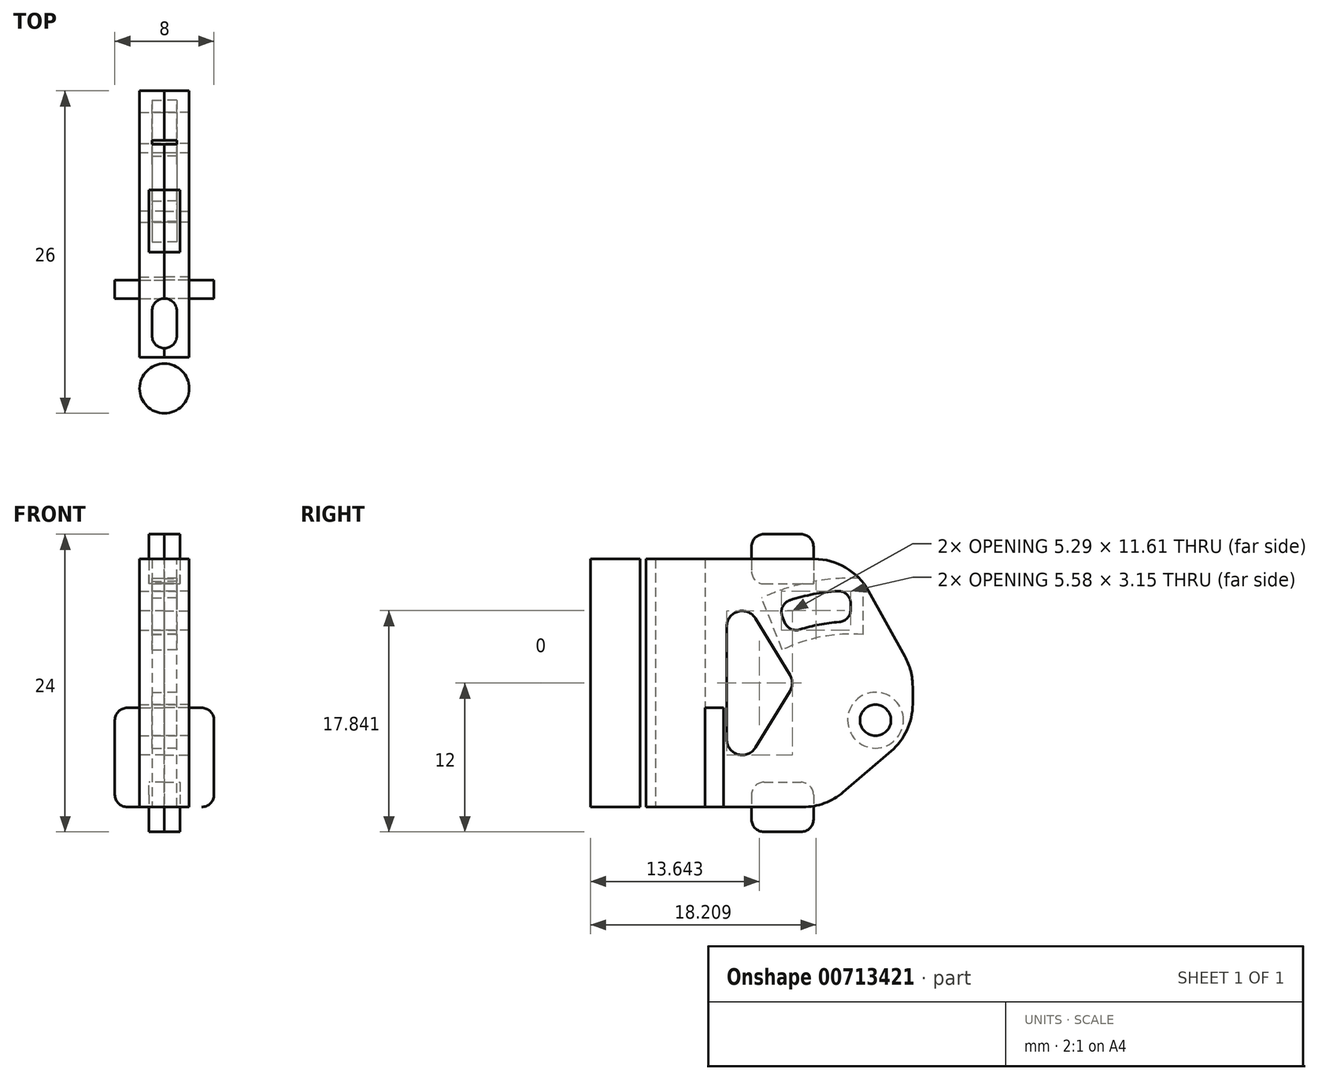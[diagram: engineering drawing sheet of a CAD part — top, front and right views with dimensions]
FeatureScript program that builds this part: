
annotation { "Feature Type Name" : "Feature", "Feature Type Description" : "" }
export const myFeature = defineFeature(function(context is Context, id is Id, definition is map)
    precondition{}
    {
        {
            var Q0;
            Q0=qCreatedBy(makeId("Right.planeOp"),FACE);
            var sketch = newSketch(context, id + "F0", { "sketchPlane" : qUnion([Q0])});
            skLineSegment(sketch, "E0.bottom", {"start": v(2.5, 0) * mm, "end": v(7, 0) * mm});
            skLineSegment(sketch, "E0.top", {"start": v(2.5, 20) * mm, "end": v(7, 20) * mm});
            skLineSegment(sketch, "E0.left", {"start": v(2.5, 0) * mm, "end": v(2.5, 20) * mm});
            skLineSegment(sketch, "E0.right", {"start": v(7, 0) * mm, "end": v(7, 20) * mm});
            skLineSegment(sketch, "E1", {"start": v(17, 0) * mm, "end": v(7, 0) * mm});
            skLineSegment(sketch, "E2", {"start": v(17, 0) * mm, "end": v(24, 6) * mm});
            skLineSegment(sketch, "E3", {"start": v(19, 20) * mm, "end": v(7, 20) * mm});
            skLineSegment(sketch, "E4", {"start": v(24, 6) * mm, "end": v(24, 11) * mm});
            skLineSegment(sketch, "E5", {"start": v(24, 11) * mm, "end": v(19, 20) * mm});
            skLineSegment(sketch, "E6", {"start": v(9, 19) * mm, "end": v(9, 1) * mm});
            skLineSegment(sketch, "E7", {"start": v(9, 1) * mm, "end": v(14.5, 10) * mm});
            skLineSegment(sketch, "E8", {"start": v(14.5, 10) * mm, "end": v(9, 19) * mm});
            skCircle(sketch, "E9", {"center": v(21, 7) * mm, "radius": 1.25 * mm});
            skArc(sketch, "E10", {"start": v(19, 17.45) * mm, "mid": v(16, 17.17) * mm, "end": v(13.1, 16.32) * mm});
            skArc(sketch, "E11", {"start": v(19, 14.95) * mm, "mid": v(16.47, 14.7) * mm, "end": v(14.03, 14) * mm});
            skLineSegment(sketch, "E12", {"start": v(19, 14.95) * mm, "end": v(19, 17.45) * mm});
            skLineSegment(sketch, "E13", {"start": v(14.03, 14) * mm, "end": v(13.1, 16.32) * mm});
            skLineSegment(sketch, "E14", {"start": v(9, 19) * mm, "end": v(9, 20) * mm, "construction": true});
            skLineSegment(sketch, "E15", {"start": v(9, 1) * mm, "end": v(9, 0) * mm, "construction": true});
            skLineSegment(sketch, "E16.bottom", {"start": v(-2.5, 0) * mm, "end": v(-8, 0) * mm});
            skLineSegment(sketch, "E16.top", {"start": v(-2.5, 17) * mm, "end": v(-8, 17) * mm});
            skLineSegment(sketch, "E16.left", {"start": v(-2.5, 0) * mm, "end": v(-2.5, 17) * mm});
            skLineSegment(sketch, "E16.right", {"start": v(-8, 0) * mm, "end": v(-8, 17) * mm});
            skLineSegment(sketch, "E17", {"start": v(-2.5, 0) * mm, "end": v(0, 0) * mm, "construction": true});
            skLineSegment(sketch, "E18", {"start": v(0, 0) * mm, "end": v(2.5, 0) * mm, "construction": true});
            skCircle(sketch, "E19.0", {"center": v(21, 7) * mm, "radius": 2.25 * mm});
            skArc(sketch, "E20.0", {"start": v(20, 18.42) * mm, "mid": v(15.81, 18.15) * mm, "end": v(11.82, 16.86) * mm});
            skLineSegment(sketch, "E20.1", {"start": v(20, 13.9) * mm, "end": v(20, 18.42) * mm});
            skArc(sketch, "E20.2", {"start": v(20, 13.9) * mm, "mid": v(16.66, 13.73) * mm, "end": v(13.48, 12.66) * mm});
            skLineSegment(sketch, "E20.3", {"start": v(13.48, 12.66) * mm, "end": v(11.82, 16.86) * mm});
            skSolve(sketch);
        }
        {
            var Q0;
            Q0=makeQuery(id+"F0.imprint","IMPRINT",FACE,{"disambiguationData":[TD([[makeQuery(id+"F0.imprint","IMPRINT",EDGE,{"derivedFrom":sQuery(id+"F0.wireOp",EDGE,"E0.right")}),-1.0]])]});
            var Q1;
            Q1=makeQuery(id+"F0.imprint","IMPRINT",FACE,{"disambiguationData":[TD([[makeQuery(id+"F0.imprint","IMPRINT",EDGE,{"derivedFrom":sQuery(id+"F0.wireOp",EDGE,"E0.bottom")}),1.0]])]});
            var Q2;
            Q2=makeQuery(id+"F0.imprint","IMPRINT",FACE,{"disambiguationData":[TD([[makeQuery(id+"F0.imprint","IMPRINT",EDGE,{"derivedFrom":sQuery(id+"F0.wireOp",EDGE,"xB6x6uVb-zKhv-ANQq-UcW5-hUPj4CPM5JXQ.bottom")}),-1.0]])]});
            var Q3;
            Q3=makeQuery(id+"F0.imprint","IMPRINT",FACE,{"disambiguationData":[TD([[makeQuery(id+"F0.imprint","IMPRINT",EDGE,{"derivedFrom":sQuery(id+"F0.wireOp",EDGE,"IHIChXXd-N6sl-k9xa-xTSY-nWWbFs0pZ4qy.bottom")}),1.0]])]});
            var Q4;
            Q4=makeQuery(id+"F0.imprint","IMPRINT",FACE,{"disambiguationData":[TD([[makeQuery(id+"F0.imprint","IMPRINT",EDGE,{"derivedFrom":sQuery(id+"F0.wireOp",EDGE,"36cd0414-5def-4b73-8972-37efab1353b10.MirrorCS")}),1.0]])]});
            var Q5;
            Q5=makeQuery(id+"F0.imprint","IMPRINT",FACE,{"disambiguationData":[TD([[makeQuery(id+"F0.imprint","IMPRINT",EDGE,{"derivedFrom":sQuery(id+"F0.wireOp",EDGE,"E10")}),-1.0]])]});
            var Q6;
            Q6=makeQuery(id+"F0.imprint","IMPRINT",FACE,{"disambiguationData":[TD([[makeQuery(id+"F0.imprint","IMPRINT",EDGE,{"derivedFrom":sQuery(id+"F0.wireOp",EDGE,"E9")}),-1.0]])]});
            extrude(context, id + "F1", {"entities" : qUnion([Q0, Q1, Q2, Q3, Q4, Q5, Q6]), "depth" : 2 * mm, "offsetDistance" : 25 * mm});
        }
        {
            var Q0;
            Q0=qCreatedBy(makeId("Top.planeOp"),FACE);
            var sketch = newSketch(context, id + "F2", { "sketchPlane" : qUnion([Q0])});
            skCircle(sketch, "E21.MirrorC", {"center": v(0, 0) * mm, "radius": 3.25 * mm});
            skCircle(sketch, "E22.MirrorC", {"center": v(0, 0) * mm, "radius": 2 * mm});
            skLineSegment(sketch, "E23.MirrorCS", {"start": v(-4, 8.75) * mm, "end": v(-4, 7.25) * mm});
            skLineSegment(sketch, "E24.MirrorCS", {"start": v(-4, 7.25) * mm, "end": v(0, 7.25) * mm});
            skLineSegment(sketch, "E25", {"start": v(0, 7.25) * mm, "end": v(0, 8.75) * mm});
            skLineSegment(sketch, "E26", {"start": v(-4, 8.75) * mm, "end": v(0, 8.75) * mm});
            skLineSegment(sketch, "E27.bottom", {"start": v(0, 11) * mm, "end": v(-1.25, 11) * mm});
            skLineSegment(sketch, "E27.top", {"start": v(0, 16) * mm, "end": v(-1.25, 16) * mm});
            skLineSegment(sketch, "E27.left", {"start": v(0, 11) * mm, "end": v(0, 16) * mm});
            skLineSegment(sketch, "E27.right", {"start": v(-1.25, 11) * mm, "end": v(-1.25, 16) * mm});
            skLineSegment(sketch, "E28.bottom", {"start": v(0, 7.25) * mm, "end": v(1, 7.25) * mm});
            skLineSegment(sketch, "E28.top", {"start": v(0, 3.1) * mm, "end": v(1, 3.1) * mm});
            skLineSegment(sketch, "E28.left", {"start": v(0, 7.25) * mm, "end": v(0, 3.1) * mm});
            skLineSegment(sketch, "E28.right", {"start": v(1, 7.25) * mm, "end": v(1, 3.1) * mm});
            skSolve(sketch);
        }
        {
            var Q0;
            Q0=makeQuery(id+"F2.imprint","IMPRINT",FACE,{"disambiguationData":[TD([[makeQuery(id+"F2.imprint","IMPRINT",EDGE,{"derivedFrom":sQuery(id+"F2.wireOp",EDGE,"E22.MirrorC")}),1.0]])]});
            var Q1;
            {var subQ2=sQuery(id+"F2.wireOp",EDGE,"d09804f8-7da6-46d8-8f41-128a26d8790d1.MirrorCS");Q1=makeQuery(id+"F2.imprint","IMPRINT",FACE,{"disambiguationData":[TD([[makeQuery(id+"F2.imprint","IMPRINT",EDGE,{"derivedFrom":subQ2}),1.0]])]});}
            extrude(context, id + "F3", {"entities" : qUnion([Q0, Q1]), "operationType" : NewBodyOperationType.ADD, "depth" : 20 * mm, "offsetDistance" : 25 * mm});
        }
        {
            var Q0;
            Q0=makeQuery(id+"F2.imprint","IMPRINT",FACE,{"disambiguationData":[TD([[makeQuery(id+"F2.imprint","IMPRINT",EDGE,{"derivedFrom":sQuery(id+"F2.wireOp",EDGE,"E23.MirrorCS")}),1.0]])]});
            extrude(context, id + "F4", {"entities" : qUnion([Q0]), "operationType" : NewBodyOperationType.ADD, "depth" : 8 * mm, "offsetDistance" : 25 * mm});
        }
        {
            var Q0;
            Q0=makeQuery(id+"F2.imprint","IMPRINT",FACE,{"disambiguationData":[TD([[makeQuery(id+"F2.imprint","IMPRINT",EDGE,{"derivedFrom":sQuery(id+"F2.wireOp",EDGE,"E27.bottom")}),-1.0]])]});
            extrude(context, id + "F5", {"entities" : qUnion([Q0]), "operationType" : NewBodyOperationType.ADD, "depth" : 2 * mm, "offsetDistance" : 25 * mm, "hasSecondDirection" : true, "secondDirectionOppositeDirection" : true, "secondDirectionDepth" : 2 * mm});
        }
        {
            var Q0;
            Q0=makeQuery(id+"F2.imprint","IMPRINT",FACE,{"disambiguationData":[TD([[makeQuery(id+"F2.imprint","IMPRINT",EDGE,{"derivedFrom":sQuery(id+"F2.wireOp",EDGE,"E27.bottom")}),-1.0]])]});
            extrude(context, id + "F6", {"entities" : qUnion([Q0]), "operationType" : NewBodyOperationType.ADD, "depth" : 22 * mm, "offsetDistance" : 25 * mm, "hasSecondDirection" : true, "secondDirectionOppositeDirection" : false, "secondDirectionDepth" : 18 * mm});
        }
        {
            var Q0;
            {var subQ4=sQuery(id+"F2.wireOp",EDGE,"E28.bottom");Q0=makeQuery(id+"F2.imprint","IMPRINT",FACE,{"disambiguationData":[TD([[makeQuery(id+"F2.imprint","IMPRINT",EDGE,{"derivedFrom":subQ4}),-1.0]])]});}
            extrude(context, id + "F7", {"entities" : qUnion([Q0]), "operationType" : NewBodyOperationType.REMOVE, "endBound" : BoundingType.THROUGH_ALL, "depth" : 25 * mm, "offsetDistance" : 25 * mm});
        }
        {
            var Q0;
            Q0=makeQuery(id+"F0.imprint","IMPRINT",FACE,{"disambiguationData":[TD([[makeQuery(id+"F0.imprint","IMPRINT",EDGE,{"derivedFrom":sQuery(id+"F0.wireOp",EDGE,"E9")}),-1.0]])]});
            var Q1;
            Q1=makeQuery(id+"F0.imprint","IMPRINT",FACE,{"disambiguationData":[TD([[makeQuery(id+"F0.imprint","IMPRINT",EDGE,{"derivedFrom":sQuery(id+"F0.wireOp",EDGE,"E10")}),-1.0]])]});
            extrude(context, id + "F8", {"entities" : qUnion([Q0, Q1]), "operationType" : NewBodyOperationType.ADD, "oppositeDirection" : true, "depth" : 1 * mm, "offsetDistance" : 25 * mm});
        }
        {
            var Q0;
            Q0=makeQuery(id+"F1.opExtrude","SWEPT_EDGE",EDGE,{"disambiguationData":[OSD([sQuery(id+"F0.wireOp",EDGE,"xB6x6uVb-zKhv-ANQq-UcW5-hUPj4CPM5JXQ.top"),sQuery(id+"F0.wireOp",EDGE,"xB6x6uVb-zKhv-ANQq-UcW5-hUPj4CPM5JXQ.left")])]});
            var Q1;
            Q1=makeQuery(id+"F1.opExtrude","SWEPT_EDGE",EDGE,{"disambiguationData":[OSD([sQuery(id+"F0.wireOp",EDGE,"xB6x6uVb-zKhv-ANQq-UcW5-hUPj4CPM5JXQ.top"),sQuery(id+"F0.wireOp",EDGE,"xB6x6uVb-zKhv-ANQq-UcW5-hUPj4CPM5JXQ.right")])]});
            var Q2;
            Q2=makeQuery(id+"F4.opExtrude","CAP_EDGE",EDGE,{"disambiguationData":[OSD([sQuery(id+"F2.wireOp",EDGE,"E23.MirrorCS")])],"isStart":false});
            var Q3;
            Q3=makeQuery(id+"F4.opExtrude","CAP_EDGE",EDGE,{"disambiguationData":[OSD([sQuery(id+"F2.wireOp",EDGE,"E23.MirrorCS")])],"isStart":true});
            var Q4;
            Q4=makeQuery(id+"F1.opExtrude","SWEPT_EDGE",EDGE,{"disambiguationData":[OSD([sQuery(id+"F0.wireOp",EDGE,"E11"),sQuery(id+"F0.wireOp",EDGE,"E13")])]});
            var Q5;
            Q5=makeQuery(id+"F1.opExtrude","SWEPT_EDGE",EDGE,{"disambiguationData":[OSD([sQuery(id+"F0.wireOp",EDGE,"E10"),sQuery(id+"F0.wireOp",EDGE,"E13")])]});
            var Q6;
            Q6=makeQuery(id+"F1.opExtrude","SWEPT_EDGE",EDGE,{"disambiguationData":[OSD([sQuery(id+"F0.wireOp",EDGE,"E10"),sQuery(id+"F0.wireOp",EDGE,"E12")])]});
            var Q7;
            Q7=makeQuery(id+"F1.opExtrude","SWEPT_EDGE",EDGE,{"disambiguationData":[OSD([sQuery(id+"F0.wireOp",EDGE,"E11"),sQuery(id+"F0.wireOp",EDGE,"E12")])]});
            var Q8;
            Q8=makeQuery(id+"F5.opExtrude","CAP_EDGE",EDGE,{"disambiguationData":[OSD([sQuery(id+"F2.wireOp",EDGE,"E27.left")])],"isStart":false});
            var Q9;
            Q9=makeQuery(id+"F5.opExtrude","CAP_EDGE",EDGE,{"disambiguationData":[OSD([sQuery(id+"F2.wireOp",EDGE,"E27.bottom")])],"isStart":false});
            var Q10;
            Q10=makeQuery(id+"F5.opExtrude","CAP_EDGE",EDGE,{"disambiguationData":[OSD([sQuery(id+"F2.wireOp",EDGE,"E27.top")])],"isStart":false});
            var Q11;
            Q11=makeQuery(id+"F5.opExtrude","CAP_EDGE",EDGE,{"disambiguationData":[OSD([sQuery(id+"F2.wireOp",EDGE,"E27.bottom")])],"isStart":true});
            var Q12;
            Q12=makeQuery(id+"F5.opExtrude","CAP_EDGE",EDGE,{"disambiguationData":[OSD([sQuery(id+"F2.wireOp",EDGE,"E27.top")])],"isStart":true});
            var Q13;
            Q13=makeQuery(id+"F6.opExtrude","CAP_EDGE",EDGE,{"disambiguationData":[OSD([sQuery(id+"F2.wireOp",EDGE,"E27.left")])],"isStart":true});
            var Q14;
            Q14=makeQuery(id+"F6.opExtrude","CAP_EDGE",EDGE,{"disambiguationData":[OSD([sQuery(id+"F2.wireOp",EDGE,"E27.bottom")])],"isStart":true});
            var Q15;
            Q15=makeQuery(id+"F6.opExtrude","CAP_EDGE",EDGE,{"disambiguationData":[OSD([sQuery(id+"F2.wireOp",EDGE,"E27.bottom")])],"isStart":false});
            var Q16;
            Q16=makeQuery(id+"F6.opExtrude","CAP_EDGE",EDGE,{"disambiguationData":[OSD([sQuery(id+"F2.wireOp",EDGE,"E27.top")])],"isStart":false});
            var Q17;
            Q17=makeQuery(id+"F7.boolean.opBoolean","COPY",EDGE,{"derivedFrom":makeQuery(id+"F7.opExtrude","SWEPT_EDGE",EDGE,{"disambiguationData":[OSD([sQuery(id+"F2.wireOp",EDGE,"E28.bottom"),sQuery(id+"F2.wireOp",EDGE,"E28.right")])]})});
            var Q18;
            Q18=makeQuery(id+"F7.boolean.opBoolean","COPY",EDGE,{"derivedFrom":makeQuery(id+"F7.opExtrude","SWEPT_EDGE",EDGE,{"disambiguationData":[OSD([sQuery(id+"F2.wireOp",EDGE,"E21.MirrorC"),sQuery(id+"F2.wireOp",EDGE,"E28.top"),sQuery(id+"F2.wireOp",EDGE,"E28.right")])]})});
            var Q19;
            Q19=makeQuery(id+"F1.opExtrude","SWEPT_EDGE",EDGE,{"disambiguationData":[OSD([sQuery(id+"F0.wireOp",EDGE,"60648e58-3a74-42ae-930e-64627e0052f30.MirrorCS"),sQuery(id+"F0.wireOp",EDGE,"cbf5a70c-ffd6-49c6-911a-603cd1f403520.MirrorCS")])]});
            var Q20;
            Q20=makeQuery(id+"F1.opExtrude","SWEPT_EDGE",EDGE,{"disambiguationData":[OSD([sQuery(id+"F0.wireOp",EDGE,"cbf5a70c-ffd6-49c6-911a-603cd1f403520.MirrorCS"),sQuery(id+"F0.wireOp",EDGE,"4e2fa409-8d6d-4920-9970-75c7dc6de36d0.MirrorCS")])]});
            var Q21;
            {var subQ0=sQuery(id+"F0.wireOp",EDGE,"E5");var subQ1=sQuery(id+"F0.wireOp",EDGE,"E20.0");Q21=makeQuery(id+"F8.boolean.opBoolean","SPLIT",EDGE,{"disambiguationData":[TD([makeQuery(id+"F1.opExtrude","SWEPT_FACE",FACE,{"disambiguationData":[OSD([subQ0])]})])],"derivedFrom":makeQuery(id+"F8.opExtrude","CAP_EDGE",EDGE,{"disambiguationData":[OSD([subQ1])],"isStart":true})});}
            var Q22;
            Q22=makeQuery(id+"F8.opExtrude","CAP_EDGE",EDGE,{"disambiguationData":[OSD([sQuery(id+"F0.wireOp",EDGE,"E19.0")])],"isStart":true});
            var Q23;
            Q23=makeQuery(id+"F1.opExtrude","SWEPT_EDGE",EDGE,{"disambiguationData":[OSD([sQuery(id+"F0.wireOp",EDGE,"E16.bottom"),sQuery(id+"F0.wireOp",EDGE,"E16.right")])]});
            var Q24;
            Q24=makeQuery(id+"F1.opExtrude","SWEPT_EDGE",EDGE,{"disambiguationData":[OSD([sQuery(id+"F0.wireOp",EDGE,"E16.top"),sQuery(id+"F0.wireOp",EDGE,"E16.right")])]});
            var Q25;
            Q25=makeQuery(id+"F8.opExtrude","CAP_EDGE",EDGE,{"disambiguationData":[OSD([sQuery(id+"F0.wireOp",EDGE,"E20.3")])],"isStart":true});
            var Q26;
            Q26=makeQuery(id+"F8.opExtrude","CAP_EDGE",EDGE,{"disambiguationData":[OSD([sQuery(id+"F0.wireOp",EDGE,"E20.2")])],"isStart":true});
            var Q27;
            Q27=makeQuery(id+"F8.opExtrude","CAP_EDGE",EDGE,{"disambiguationData":[OSD([sQuery(id+"F0.wireOp",EDGE,"E20.1")])],"isStart":true});
            fillet(context, id + "F9", {"entities" : qUnion([Q0, Q1, Q2, Q3, Q4, Q5, Q6, Q7, Q8, Q9, Q10, Q11, Q12, Q13, Q14, Q15, Q16, Q17, Q18, Q19, Q20, Q21, Q22, Q23, Q24, Q25, Q26, Q27]), "radius" : 1 * mm, "tangentPropagation" : true, "allowEdgeOverflow" : false});
        }
        {
            var Q0;
            Q0=makeQuery(id+"F1.opExtrude","SWEPT_EDGE",EDGE,{"disambiguationData":[OSD([sQuery(id+"F0.wireOp",EDGE,"E6"),sQuery(id+"F0.wireOp",EDGE,"E8")])]});
            var Q1;
            Q1=makeQuery(id+"F1.opExtrude","SWEPT_EDGE",EDGE,{"disambiguationData":[OSD([sQuery(id+"F0.wireOp",EDGE,"E7"),sQuery(id+"F0.wireOp",EDGE,"E8")])]});
            var Q2;
            Q2=makeQuery(id+"F1.opExtrude","SWEPT_EDGE",EDGE,{"disambiguationData":[OSD([sQuery(id+"F0.wireOp",EDGE,"E6"),sQuery(id+"F0.wireOp",EDGE,"E7")])]});
            fillet(context, id + "F10", {"entities" : qUnion([Q0, Q1, Q2]), "radius" : 1.25 * mm, "tangentPropagation" : true, "allowEdgeOverflow" : false});
        }
        {
            var Q0;
            Q0=makeQuery(id+"F3.boolean.opBoolean","INTERSECT",EDGE,{"derivedFrom":[makeQuery(id+"F1.opExtrude","CAP_FACE",FACE,{"disambiguationData":[OSD([sQuery(id+"F0.wireOp",EDGE,"E0.bottom"),sQuery(id+"F0.wireOp",EDGE,"E0.top"),sQuery(id+"F0.wireOp",EDGE,"E0.left"),sQuery(id+"F0.wireOp",EDGE,"E1"),sQuery(id+"F0.wireOp",EDGE,"E2"),sQuery(id+"F0.wireOp",EDGE,"E3"),sQuery(id+"F0.wireOp",EDGE,"E4"),sQuery(id+"F0.wireOp",EDGE,"E5"),sQuery(id+"F0.wireOp",EDGE,"E6"),sQuery(id+"F0.wireOp",EDGE,"E7"),sQuery(id+"F0.wireOp",EDGE,"E8"),sQuery(id+"F0.wireOp",EDGE,"E9"),sQuery(id+"F0.wireOp",EDGE,"E10"),sQuery(id+"F0.wireOp",EDGE,"E11"),sQuery(id+"F0.wireOp",EDGE,"E12"),sQuery(id+"F0.wireOp",EDGE,"E13")])],"isStart":false}),makeQuery(id+"F3.opExtrude","SWEPT_FACE",FACE,{"disambiguationData":[OSD([sQuery(id+"F2.wireOp",EDGE,"E21.MirrorC")])]})]});
            var Q1;
            Q1=makeQuery(id+"F3.boolean.opBoolean","INTERSECT",EDGE,{"derivedFrom":[makeQuery(id+"F1.opExtrude","CAP_FACE",FACE,{"disambiguationData":[OSD([sQuery(id+"F0.wireOp",EDGE,"E16.bottom"),sQuery(id+"F0.wireOp",EDGE,"E16.top"),sQuery(id+"F0.wireOp",EDGE,"E16.left"),sQuery(id+"F0.wireOp",EDGE,"E16.right")])],"isStart":true}),makeQuery(id+"F3.opExtrude","SWEPT_FACE",FACE,{"disambiguationData":[OSD([sQuery(id+"F2.wireOp",EDGE,"E21.MirrorC")])]})]});
            var Q2;
            Q2=makeQuery(id+"F3.boolean.opBoolean","INTERSECT",EDGE,{"derivedFrom":[makeQuery(id+"F1.opExtrude","CAP_FACE",FACE,{"disambiguationData":[OSD([sQuery(id+"F0.wireOp",EDGE,"E16.bottom"),sQuery(id+"F0.wireOp",EDGE,"E16.top"),sQuery(id+"F0.wireOp",EDGE,"E16.left"),sQuery(id+"F0.wireOp",EDGE,"E16.right")])],"isStart":false}),makeQuery(id+"F3.opExtrude","SWEPT_FACE",FACE,{"disambiguationData":[OSD([sQuery(id+"F2.wireOp",EDGE,"E21.MirrorC")])]})]});
            var Q3;
            Q3=makeQuery(id+"F1.opExtrude","SWEPT_EDGE",EDGE,{"disambiguationData":[OSD([sQuery(id+"F0.wireOp",EDGE,"E3"),sQuery(id+"F0.wireOp",EDGE,"E5")])]});
            var Q4;
            Q4=makeQuery(id+"F1.opExtrude","SWEPT_EDGE",EDGE,{"disambiguationData":[OSD([sQuery(id+"F0.wireOp",EDGE,"E4"),sQuery(id+"F0.wireOp",EDGE,"E5")])]});
            var Q5;
            Q5=makeQuery(id+"F1.opExtrude","SWEPT_EDGE",EDGE,{"disambiguationData":[OSD([sQuery(id+"F0.wireOp",EDGE,"E2"),sQuery(id+"F0.wireOp",EDGE,"E4")])]});
            var Q6;
            Q6=makeQuery(id+"F1.opExtrude","SWEPT_EDGE",EDGE,{"disambiguationData":[OSD([sQuery(id+"F0.wireOp",EDGE,"E1"),sQuery(id+"F0.wireOp",EDGE,"E2")])]});
            fillet(context, id + "F11", {"entities" : qUnion([Q0, Q1, Q2, Q3, Q4, Q5, Q6]), "radius" : 5 * mm, "tangentPropagation" : true, "allowEdgeOverflow" : false});
        }
        {
            var Q0;
            Q0=makeQuery(id+"F1.opExtrude","SWEPT_BODY",BODY,{"disambiguationData":[OSD([sQuery(id+"F0.wireOp",EDGE,"E0.bottom"),sQuery(id+"F0.wireOp",EDGE,"E0.top"),sQuery(id+"F0.wireOp",EDGE,"E0.left"),sQuery(id+"F0.wireOp",EDGE,"E1"),sQuery(id+"F0.wireOp",EDGE,"E2"),sQuery(id+"F0.wireOp",EDGE,"E3"),sQuery(id+"F0.wireOp",EDGE,"E4"),sQuery(id+"F0.wireOp",EDGE,"E5"),sQuery(id+"F0.wireOp",EDGE,"E6"),sQuery(id+"F0.wireOp",EDGE,"E7"),sQuery(id+"F0.wireOp",EDGE,"E8"),sQuery(id+"F0.wireOp",EDGE,"E9"),sQuery(id+"F0.wireOp",EDGE,"E10"),sQuery(id+"F0.wireOp",EDGE,"E11"),sQuery(id+"F0.wireOp",EDGE,"E12"),sQuery(id+"F0.wireOp",EDGE,"E13")])]});
            var Q1;
            Q1=qCreatedBy(makeId("Right.planeOp"),FACE);
            mirror(context, id + "F12", {"entities" : qUnion([Q0]), "mirrorPlane" : qUnion([Q1])});
        }
    });
